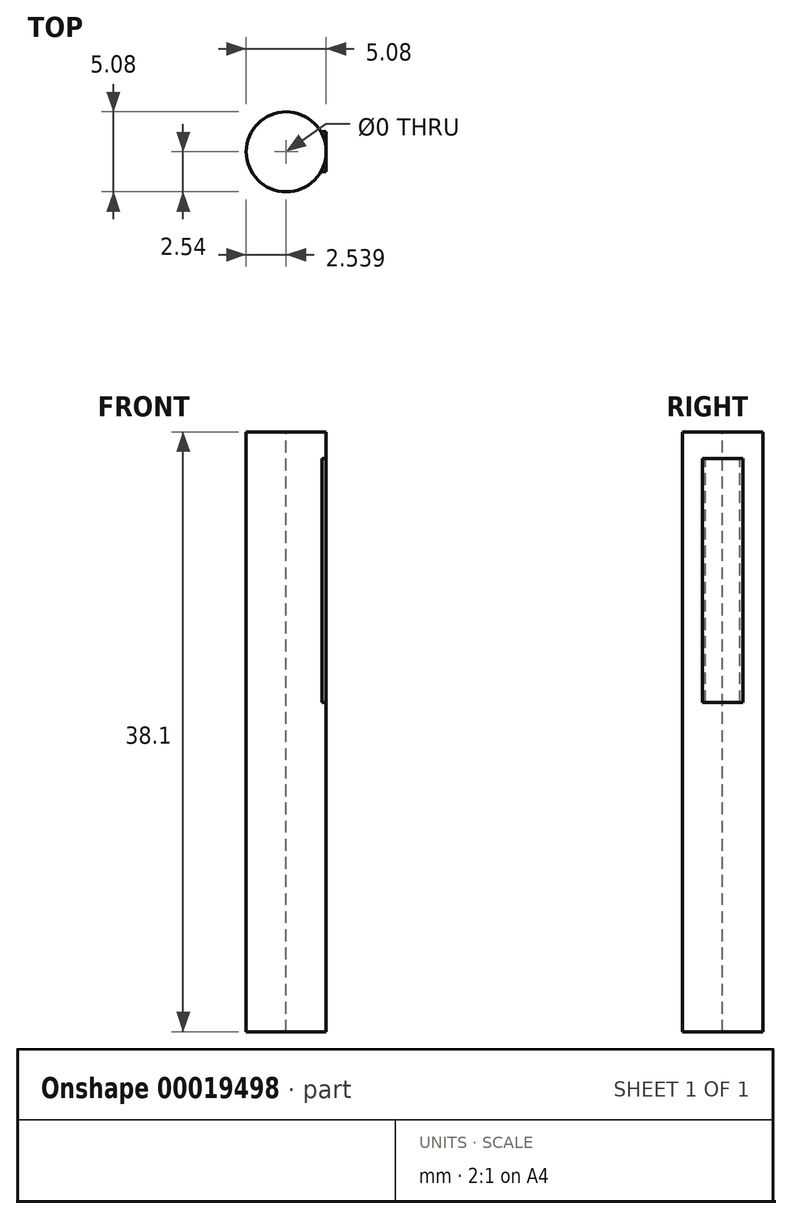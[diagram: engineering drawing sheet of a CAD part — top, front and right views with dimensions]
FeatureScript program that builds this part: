
annotation { "Feature Type Name" : "Feature", "Feature Type Description" : "" }
export const myFeature = defineFeature(function(context is Context, id is Id, definition is map)
    precondition{}
    {
        {
            var Q0;
            Q0=qCreatedBy(makeId("Front.planeOp"),FACE);
            var sketch = newSketch(context, id + "F0", { "sketchPlane" : qUnion([Q0])});
            skLineSegment(sketch, "E0", {"start": v(-37.46, 21.33) * mm, "end": v(-37.46, -29.47) * mm, "construction": true});
            skLineSegment(sketch, "E1", {"start": v(-37.46, -29.47) * mm, "end": v(13.34, -29.47) * mm, "construction": true});
            skLineSegment(sketch, "E2", {"start": v(13.34, -29.47) * mm, "end": v(13.34, 21.33) * mm, "construction": true});
            skLineSegment(sketch, "E3", {"start": v(13.34, 21.33) * mm, "end": v(-37.46, 21.33) * mm, "construction": true});
            skLineSegment(sketch, "E4.bottom", {"start": v(-2.54, 17.2) * mm, "end": v(0, 17.2) * mm});
            skLineSegment(sketch, "E4.top", {"start": v(-2.54, -20.9) * mm, "end": v(0, -20.9) * mm});
            skLineSegment(sketch, "E4.left", {"start": v(-2.54, 17.2) * mm, "end": v(-2.54, -20.9) * mm});
            skLineSegment(sketch, "E4.right", {"start": v(0, 17.2) * mm, "end": v(0, -20.9) * mm});
            skLineSegment(sketch, "E5", {"start": v(0, 0) * mm, "end": v(0, 17.2) * mm, "construction": true});
            skSolve(sketch);
        }
        {
            var Q0;
            Q0=makeQuery(id+"F0.imprint","IMPRINT",FACE,{"disambiguationData":[TD([[makeQuery(id+"F0.imprint","IMPRINT",EDGE,{"derivedFrom":sQuery(id+"F0.wireOp",EDGE,"E4.bottom")}),-1.0]])]});
            var Q1;
            Q1=sQuery(id+"F0.wireOp",EDGE,"E4.left");
            revolve(context, id + "F1", {"entities" : qUnion([Q0]), "axis" : qUnion([Q1]), "revolveType" : RevolveType.FULL});
        }
        {
            var Q0;
            Q0=qCreatedBy(makeId("Top.planeOp"),FACE);
            var sketch = newSketch(context, id + "F2", { "sketchPlane" : qUnion([Q0])});
            skLineSegment(sketch, "E6.bottom", {"start": v(4.03, 2.5) * mm, "end": v(4.03, 2.5) * mm});
            skLineSegment(sketch, "E6.top", {"start": v(4.03, -2.5) * mm, "end": v(4.03, -2.5) * mm});
            skLineSegment(sketch, "E6.left", {"start": v(0, 0) * mm, "end": v(0, 0) * mm});
            skLineSegment(sketch, "E6.right", {"start": v(0, 2.5) * mm, "end": v(0, -2.5) * mm});
            skCircle(sketch, "E7", {"center": v(2.8, 0) * mm, "radius": 2.8 * mm});
            skPoint(sketch, "E7.first.point", {"position": v(1.84, 2.63) * mm});
            skPoint(sketch, "E7.second.point", {"position": v(3.72, -2.64) * mm});
            skPoint(sketch, "E7.third.point", {"position": v(5.59, -0.08) * mm});
            skLineSegment(sketch, "E8", {"start": v(0, 0) * mm, "end": v(2.8, 0) * mm});
            skLineSegment(sketch, "E9", {"start": v(2.8, 0) * mm, "end": v(2.8, 2.8) * mm});
            skLineSegment(sketch, "E10", {"start": v(2.8, 0) * mm, "end": v(2.8, -2.8) * mm});
            skLineSegment(sketch, "E11", {"start": v(4.03, 2.5) * mm, "end": v(0, 2.5) * mm});
            skLineSegment(sketch, "E12", {"start": v(0, 2.5) * mm, "end": v(4.03, 2.5) * mm});
            skLineSegment(sketch, "E13", {"start": v(0, 0) * mm, "end": v(0, 2.5) * mm});
            skLineSegment(sketch, "E14", {"start": v(0, 0) * mm, "end": v(0, -2.5) * mm});
            skLineSegment(sketch, "E15", {"start": v(0, -2.5) * mm, "end": v(4.03, -2.5) * mm});
            skLineSegment(sketch, "E16", {"start": v(4.03, -2.5) * mm, "end": v(0, -2.5) * mm});
            skPoint(sketch, "E17.orphan", {"position": v(0, 2.5) * mm});
            skPoint(sketch, "E18.orphan", {"position": v(0, -2.5) * mm});
            skSolve(sketch);
        }
        {
            var Q0;
            Q0=sQuery(id+"F2.wireOp",EDGE,"E6.right");
            extrude(context, id + "F3", {"bodyType" : ToolBodyType.SURFACE, "surfaceEntities" : qUnion([Q0]), "depth" : 0.03 * mm});
        }
        {
            var Q0;
            Q0=makeQuery(id+"F3.opExtrude","SWEPT_FACE",FACE,{"disambiguationData":[OSD([sQuery(id+"F2.wireOp",EDGE,"E6.right")])]});
            var sketch = newSketch(context, id + "F4", { "sketchPlane" : qUnion([Q0])});
            skLineSegment(sketch, "E19", {"start": v(-1.27, 15.52) * mm, "end": v(-1.27, 0.03) * mm});
            skLineSegment(sketch, "E20", {"start": v(-1.27, 0.03) * mm, "end": v(1.27, 0.03) * mm});
            skLineSegment(sketch, "E21", {"start": v(1.27, 0.03) * mm, "end": v(1.27, 15.52) * mm});
            skLineSegment(sketch, "E22", {"start": v(1.27, 15.52) * mm, "end": v(-1.27, 15.52) * mm});
            skLineSegment(sketch, "E23", {"start": v(-2.54, 15.52) * mm, "end": v(2.54, 15.52) * mm, "construction": true});
            skLineSegment(sketch, "E24", {"start": v(-2.54, 15.52) * mm, "end": v(-1.27, 15.52) * mm, "construction": true});
            skLineSegment(sketch, "E25", {"start": v(1.27, 15.52) * mm, "end": v(2.54, 15.52) * mm, "construction": true});
            skLineSegment(sketch, "E26", {"start": v(2.54, 15.52) * mm, "end": v(2.5, 0.03) * mm});
            skLineSegment(sketch, "E27", {"start": v(2.5, 0.03) * mm, "end": v(-2.5, 0) * mm});
            skLineSegment(sketch, "E28", {"start": v(-2.5, 0) * mm, "end": v(-2.54, 15.52) * mm});
            skLineSegment(sketch, "E29", {"start": v(12.92, 12.1) * mm, "end": v(12.92, 10.4) * mm, "construction": true});
            skSolve(sketch);
        }
        {
            var Q0;
            Q0=makeQuery(id+"F4.imprint","IMPRINT",FACE,{"disambiguationData":[TD([[makeQuery(id+"F4.imprint","IMPRINT",EDGE,{"derivedFrom":sQuery(id+"F4.wireOp",EDGE,"E19")}),1.0]])]});
            extrude(context, id + "F5", {"entities" : qUnion([Q0]), "operationType" : NewBodyOperationType.ADD, "depth" : 0.25 * mm});
        }
    });
